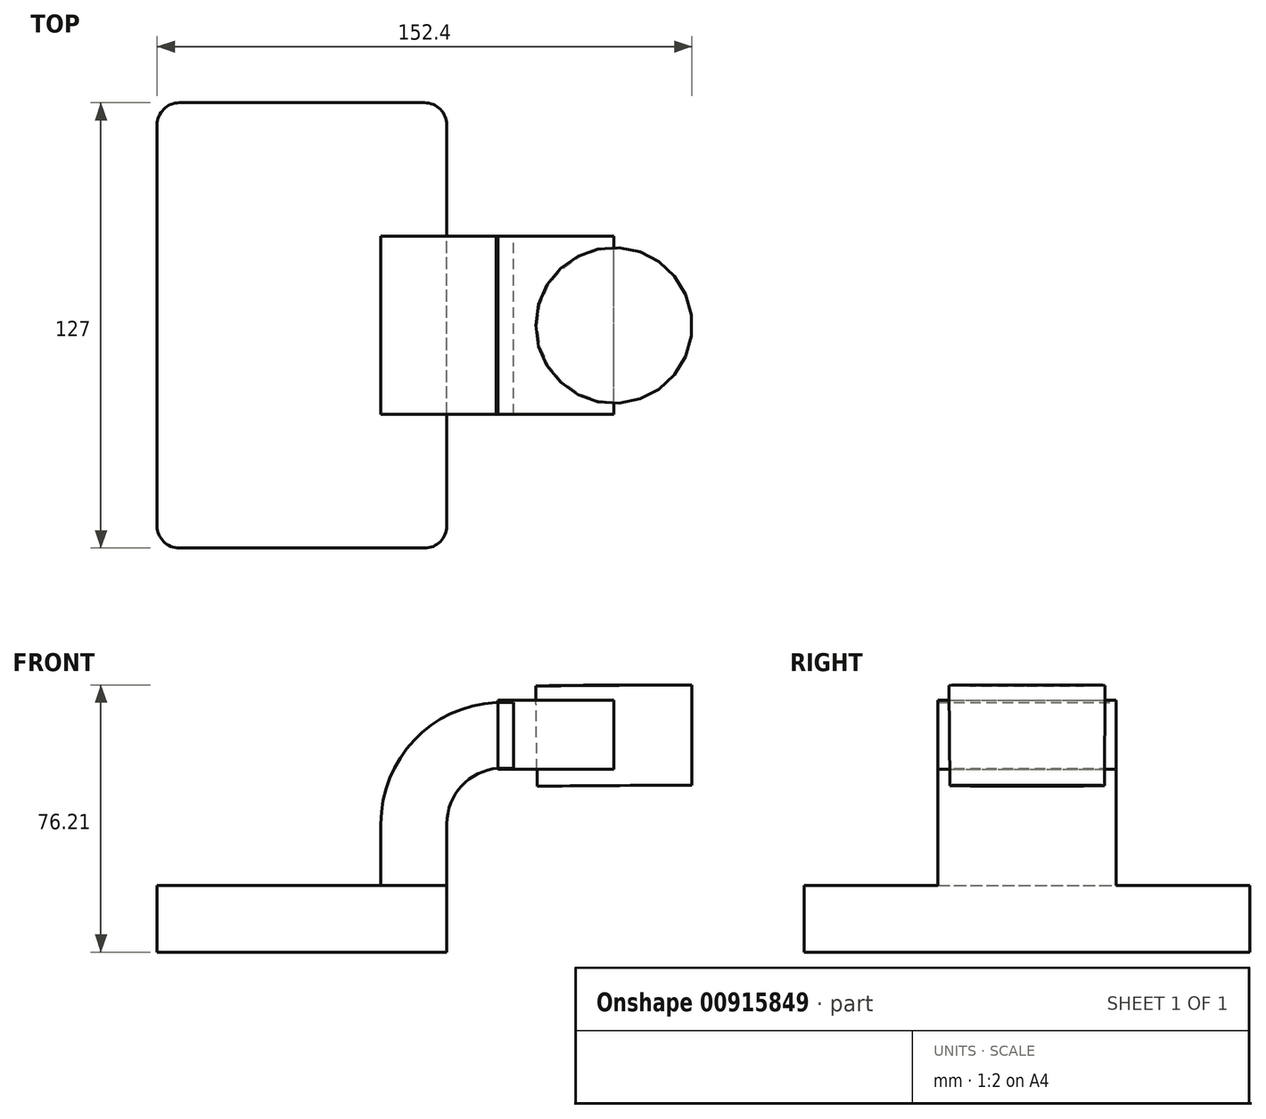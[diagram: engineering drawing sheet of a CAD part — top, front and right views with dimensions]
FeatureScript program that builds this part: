
annotation { "Feature Type Name" : "Feature", "Feature Type Description" : "" }
export const myFeature = defineFeature(function(context is Context, id is Id, definition is map)
    precondition{}
    {
        {
            var Q0;
            Q0=qCreatedBy(makeId("Front.planeOp"),FACE);
            var sketch = newSketch(context, id + "F0", { "sketchPlane" : qUnion([Q0])});
            skLineSegment(sketch, "E0.bottom", {"start": v(-41.28, -9.53) * mm, "end": v(41.28, -9.53) * mm});
            skLineSegment(sketch, "E0.top", {"start": v(-41.28, 9.52) * mm, "end": v(41.28, 9.52) * mm});
            skLineSegment(sketch, "E0.left", {"start": v(-41.28, -9.53) * mm, "end": v(-41.28, 9.52) * mm});
            skLineSegment(sketch, "E0.right", {"start": v(41.28, -9.53) * mm, "end": v(41.28, 9.52) * mm});
            skPoint(sketch, "E0.middle", {"position": v(0, 0) * mm});
            skLineSegment(sketch, "E1", {"start": v(41.28, 9.52) * mm, "end": v(41.28, 27.05) * mm});
            skLineSegment(sketch, "E2.bottom", {"start": v(111.12, 66.68) * mm, "end": v(60.32, 66.68) * mm});
            skLineSegment(sketch, "E2.top", {"start": v(111.12, 38.1) * mm, "end": v(60.32, 38.1) * mm});
            skLineSegment(sketch, "E2.left", {"start": v(111.12, 66.68) * mm, "end": v(111.12, 38.1) * mm});
            skLineSegment(sketch, "E2.right", {"start": v(60.32, 66.68) * mm, "end": v(60.33, 38.1) * mm});
            skPoint(sketch, "E2.middle", {"position": v(85.73, 52.39) * mm});
            skArc(sketch, "E3", {"start": v(41.27, 27.05) * mm, "mid": v(45.49, 37.82) * mm, "end": v(55.89, 42.88) * mm});
            skLineSegment(sketch, "E4", {"start": v(55.89, 42.88) * mm, "end": v(88.88, 42.88) * mm});
            skLineSegment(sketch, "E5.0", {"start": v(55.29, 61.67) * mm, "end": v(88.88, 61.67) * mm});
            skArc(sketch, "E5.1", {"start": v(22.48, 27.05) * mm, "mid": v(31.98, 50.9) * mm, "end": v(55.29, 61.67) * mm});
            skLineSegment(sketch, "E5.2", {"start": v(22.48, 9.52) * mm, "end": v(22.48, 27.05) * mm});
            skLineSegment(sketch, "E6", {"start": v(89.07, 38.1) * mm, "end": v(88.88, 66.68) * mm});
            skFitSpline(sketch, "E7", {"points": [v(-41.28, 9.53) * mm, v(55.29, 61.67) * mm], "startDerivative": vector(-0.93, 71.2) * mm, "endDerivative": vector(191.63, 0.1) * mm});
            skSolve(sketch);
        }
        {
            var Q0;
            Q0=makeQuery(id+"F0.imprint","IMPRINT",FACE,{"disambiguationData":[TD([[makeQuery(id+"F0.imprint","IMPRINT",EDGE,{"derivedFrom":sQuery(id+"F0.wireOp",EDGE,"E0.bottom")}),1.0]])]});
            extrude(context, id + "F1", {"entities" : qUnion([Q0]), "endBound" : BoundingType.SYMMETRIC, "depth" : 127 * mm, "offsetDistance" : 25.4 * mm});
        }
        {
            var Q0;
            {var subQ1=sQuery(id+"F0.wireOp",EDGE,"E1");Q0=makeQuery(id+"F0.imprint","IMPRINT",FACE,{"disambiguationData":[TD([[makeQuery(id+"F0.imprint","IMPRINT",EDGE,{"derivedFrom":subQ1}),1.0]])]});}
            extrude(context, id + "F2", {"entities" : qUnion([Q0]), "operationType" : NewBodyOperationType.ADD, "endBound" : BoundingType.SYMMETRIC, "depth" : 50.8 * mm, "offsetDistance" : 25.4 * mm});
        }
        {
            var Q0;
            Q0=makeQuery(id+"F0.imprint","IMPRINT",FACE,{"disambiguationData":[TD([[makeQuery(id+"F0.imprint","IMPRINT",EDGE,{"derivedFrom":sQuery(id+"F0.wireOp",EDGE,"E5.1")}),1.0]])]});
            extrude(context, id + "F3", {"entities" : qUnion([Q0]), "operationType" : NewBodyOperationType.ADD, "endBound" : BoundingType.SYMMETRIC, "depth" : 15.88 * mm, "offsetDistance" : 25.4 * mm});
        }
        {
            var Q0;
            Q0=makeQuery(id+"F1.opExtrude","CAP_EDGE",EDGE,{"disambiguationData":[OSD([sQuery(id+"F0.wireOp",EDGE,"E0.right")])],"isStart":false});
            var Q1;
            Q1=makeQuery(id+"F1.opExtrude","CAP_EDGE",EDGE,{"disambiguationData":[OSD([sQuery(id+"F0.wireOp",EDGE,"E0.left")])],"isStart":false});
            var Q2;
            Q2=makeQuery(id+"F1.opExtrude","CAP_EDGE",EDGE,{"disambiguationData":[OSD([sQuery(id+"F0.wireOp",EDGE,"E0.right")])],"isStart":true});
            var Q3;
            Q3=makeQuery(id+"F1.opExtrude","CAP_EDGE",EDGE,{"disambiguationData":[OSD([sQuery(id+"F0.wireOp",EDGE,"E0.left")])],"isStart":true});
            fillet(context, id + "F4", {"entities" : qUnion([Q0, Q1, Q2, Q3]), "radius" : 6.35 * mm, "tangentPropagation" : true, "allowEdgeOverflow" : false});
        }
        {
            var Q0;
            {var subQ0=sQuery(id+"F0.wireOp",EDGE,"E2.left");Q0=makeQuery(id+"F0.imprint","IMPRINT",FACE,{"disambiguationData":[TD([[makeQuery(id+"F0.imprint","IMPRINT",EDGE,{"derivedFrom":subQ0}),-1.0]])]});}
            var Q1;
            Q1=sQuery(id+"F0.wireOp",EDGE,"E6");
            revolve(context, id + "F5", {"surfaceOperationType" : NewSurfaceOperationType.NEW, "entities" : qUnion([Q0]), "axis" : qUnion([Q1]), "revolveType" : RevolveType.FULL});
        }
        {
            var Q0;
            Q0=qCreatedBy(makeId("Front.planeOp"),FACE);
            var sketch = newSketch(context, id + "F6", { "sketchPlane" : qUnion([Q0])});
            skLineSegment(sketch, "E8.bottom", {"start": v(55.9, 62.36) * mm, "end": v(88.9, 62.36) * mm});
            skLineSegment(sketch, "E8.top", {"start": v(55.9, 42.56) * mm, "end": v(88.9, 42.56) * mm});
            skLineSegment(sketch, "E8.left", {"start": v(55.9, 62.36) * mm, "end": v(55.9, 42.56) * mm});
            skLineSegment(sketch, "E8.right", {"start": v(88.9, 62.36) * mm, "end": v(88.9, 42.56) * mm});
            skSolve(sketch);
        }
        {
            var Q0;
            Q0=makeQuery(id+"F6.imprint","IMPRINT",FACE,{"disambiguationData":[TD([[makeQuery(id+"F6.imprint","IMPRINT",EDGE,{"derivedFrom":sQuery(id+"F6.wireOp",EDGE,"E8.bottom")}),-1.0]])]});
            extrude(context, id + "F7", {"entities" : qUnion([Q0]), "endBound" : BoundingType.SYMMETRIC, "depth" : 50.8 * mm, "offsetDistance" : 25.4 * mm});
        }
    });
